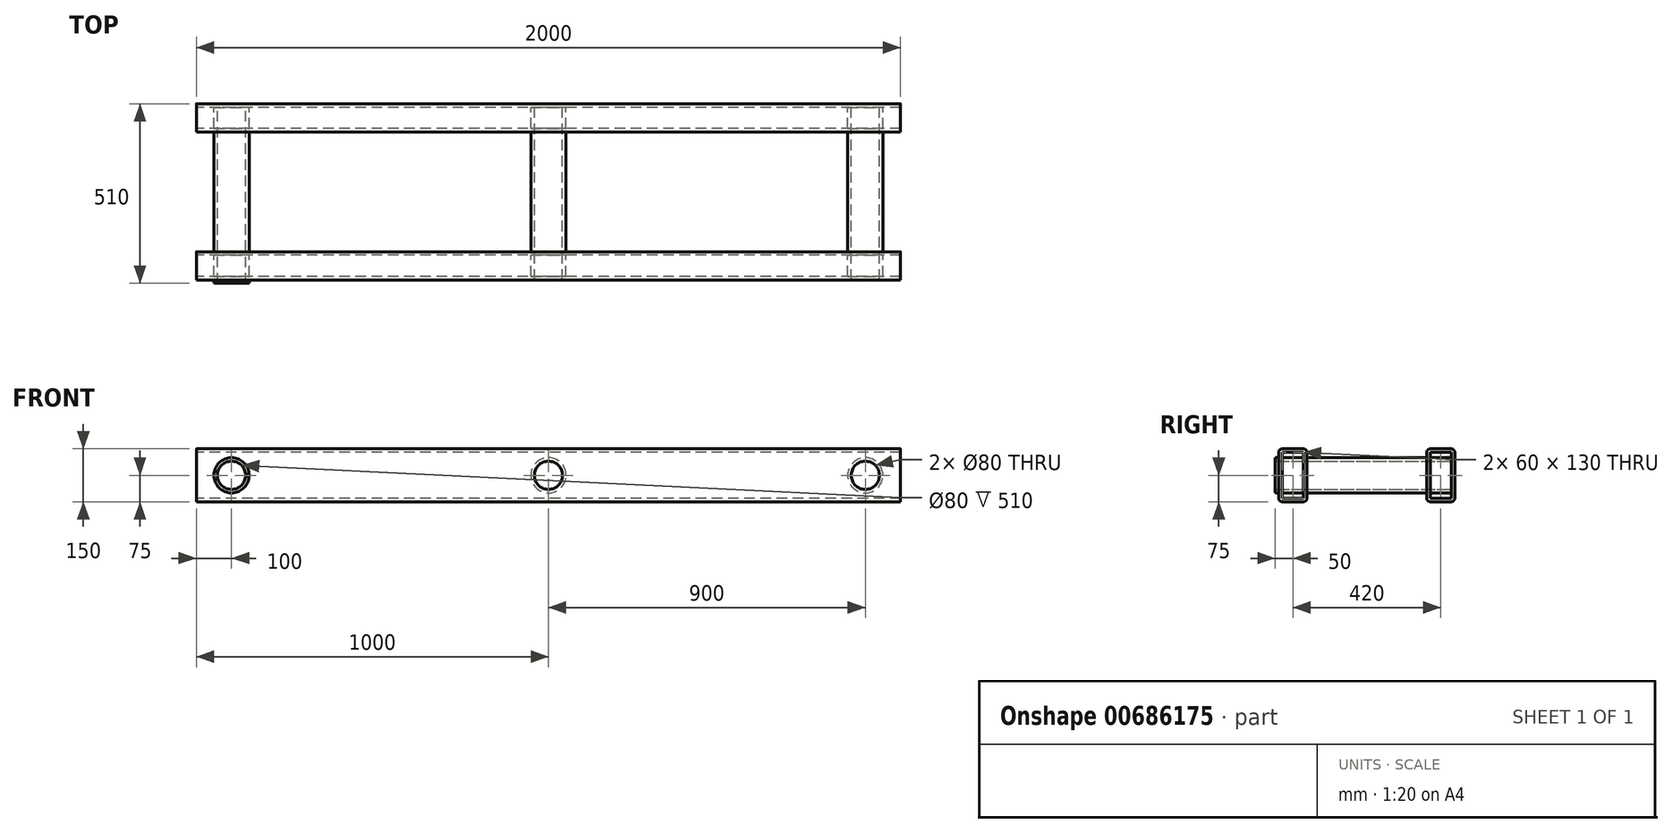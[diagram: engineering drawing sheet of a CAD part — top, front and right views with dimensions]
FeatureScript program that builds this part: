
annotation { "Feature Type Name" : "Feature", "Feature Type Description" : "" }
export const myFeature = defineFeature(function(context is Context, id is Id, definition is map)
    precondition{}
    {
        {
            var Q0;
            Q0=qCreatedBy(makeId("Right.planeOp"),FACE);
            var sketch = newSketch(context, id + "F0", { "sketchPlane" : qUnion([Q0])});
            skLineSegment(sketch, "E0.rect.bottom", {"start": v(-180, -75) * mm, "end": v(-240, -75) * mm});
            skLineSegment(sketch, "E0.rect.top", {"start": v(-180, 75) * mm, "end": v(-240, 75) * mm});
            skLineSegment(sketch, "E0.rect.left", {"start": v(-170, -65) * mm, "end": v(-170, 65) * mm});
            skLineSegment(sketch, "E0.rect.right", {"start": v(-250, -65) * mm, "end": v(-250, 65) * mm});
            skPoint(sketch, "E0.rect.middle", {"position": v(-210, 0) * mm});
            skPoint(sketch, "E1.visualSharp", {"position": v(-250, 75) * mm});
            skArc(sketch, "E1.filletArc", {"start": v(-240, 75) * mm, "mid": v(-247.07, 72.07) * mm, "end": v(-250, 65) * mm});
            skPoint(sketch, "E2.visualSharp", {"position": v(-170, 75) * mm});
            skArc(sketch, "E2.filletArc", {"start": v(-170, 65) * mm, "mid": v(-172.93, 72.07) * mm, "end": v(-180, 75) * mm});
            skPoint(sketch, "E3.visualSharp", {"position": v(-170, -75) * mm});
            skArc(sketch, "E3.filletArc", {"start": v(-180, -75) * mm, "mid": v(-172.93, -72.07) * mm, "end": v(-170, -65) * mm});
            skPoint(sketch, "E4.visualSharp", {"position": v(-250, -75) * mm});
            skArc(sketch, "E4.filletArc", {"start": v(-250, -65) * mm, "mid": v(-247.07, -72.07) * mm, "end": v(-240, -75) * mm});
            skLineSegment(sketch, "E5.0", {"start": v(-180, 65) * mm, "end": v(-240, 65) * mm});
            skLineSegment(sketch, "E5.1", {"start": v(-180, -65) * mm, "end": v(-180, 65) * mm});
            skLineSegment(sketch, "E5.2", {"start": v(-180, -65) * mm, "end": v(-240, -65) * mm});
            skLineSegment(sketch, "E5.3", {"start": v(-240, -65) * mm, "end": v(-240, 65) * mm});
            skArc(sketch, "E6.MirrorCS", {"start": v(240, 75) * mm, "mid": v(247.07, 72.07) * mm, "end": v(250, 65) * mm});
            skArc(sketch, "E7.MirrorCS", {"start": v(170, 65) * mm, "mid": v(172.93, 72.07) * mm, "end": v(180, 75) * mm});
            skArc(sketch, "E8.MirrorCS", {"start": v(250, -65) * mm, "mid": v(247.07, -72.07) * mm, "end": v(240, -75) * mm});
            skArc(sketch, "E9.MirrorCS", {"start": v(180, -75) * mm, "mid": v(172.93, -72.07) * mm, "end": v(170, -65) * mm});
            skLineSegment(sketch, "E10.MirrorCS", {"start": v(180, -75) * mm, "end": v(240, -75) * mm});
            skPoint(sketch, "E11.MirrorP", {"position": v(250, -75) * mm});
            skLineSegment(sketch, "E12.MirrorCS", {"start": v(240, -65) * mm, "end": v(240, 65) * mm});
            skPoint(sketch, "E13.MirrorP", {"position": v(170, 75) * mm});
            skPoint(sketch, "E14.MirrorP", {"position": v(250, 75) * mm});
            skLineSegment(sketch, "E15.MirrorCS", {"start": v(180, -65) * mm, "end": v(240, -65) * mm});
            skPoint(sketch, "E16.MirrorP", {"position": v(210, 0) * mm});
            skLineSegment(sketch, "E17.MirrorCS", {"start": v(180, -65) * mm, "end": v(180, 65) * mm});
            skLineSegment(sketch, "E18.MirrorCS", {"start": v(180, 75) * mm, "end": v(240, 75) * mm});
            skPoint(sketch, "E19.MirrorP", {"position": v(170, -75) * mm});
            skLineSegment(sketch, "E20.MirrorCS", {"start": v(170, -65) * mm, "end": v(170, 65) * mm});
            skLineSegment(sketch, "E21.MirrorCS", {"start": v(180, 65) * mm, "end": v(240, 65) * mm});
            skLineSegment(sketch, "E22.MirrorCS", {"start": v(250, -65) * mm, "end": v(250, 65) * mm});
            skSolve(sketch);
        }
        {
            var Q0;
            Q0=qSketchRegion(id+"F0",true);
            extrude(context, id + "F1", {"entities" : qUnion([Q0]), "endBound" : BoundingType.SYMMETRIC, "depth" : 2000 * mm});
        }
        {
            var Q0;
            Q0=qCreatedBy(makeId("Front.planeOp"),FACE);
            var sketch = newSketch(context, id + "F2", { "sketchPlane" : qUnion([Q0])});
            skCircle(sketch, "E23", {"center": v(900, 0) * mm, "radius": 50 * mm});
            skCircle(sketch, "E24", {"center": v(900, 0) * mm, "radius": 40 * mm});
            skCircle(sketch, "E25.1.0.0", {"center": v(0, 0) * mm, "radius": 50 * mm});
            skCircle(sketch, "E25.1.0.1", {"center": v(0, 0) * mm, "radius": 40 * mm});
            skCircle(sketch, "E25.2.0.0", {"center": v(-900, 0) * mm, "radius": 50 * mm});
            skCircle(sketch, "E25.2.0.1", {"center": v(-900, 0) * mm, "radius": 40 * mm});
            skLineSegment(sketch, "E25.direction1", {"start": v(900, 0) * mm, "end": v(0, 0) * mm, "construction": true});
            skSolve(sketch);
        }
        {
            var Q0;
            Q0=qSketchRegion(id+"F2",true);
            var Q1;
            Q1=makeQuery(id+"F1.opExtrude","SWEPT_FACE",FACE,{"disambiguationData":[OSD([sQuery(id+"F0.wireOp",EDGE,"E0.rect.right")])]});
            var Q2;
            Q2=makeQuery(id+"F1.opExtrude","SWEPT_FACE",FACE,{"disambiguationData":[OSD([sQuery(id+"F0.wireOp",EDGE,"E22.MirrorCS")])]});
            extrude(context, id + "F3", {"entities" : qUnion([Q0]), "operationType" : NewBodyOperationType.ADD, "endBound" : BoundingType.UP_TO_SURFACE, "endBoundEntityFace" : qUnion([Q1]), "depth" : 25 * mm, "hasSecondDirection" : true, "secondDirectionBound" : SecondDirectionBoundingType.UP_TO_SURFACE, "secondDirectionOppositeDirection" : true, "secondDirectionBoundEntityFace" : qUnion([Q2]), "secondDirectionDepth" : 25 * mm});
        }
        {
            var Q0;
            Q0=makeQuery(id+"F2.imprint","IMPRINT",FACE,{"disambiguationData":[TD([[makeQuery(id+"F2.imprint","IMPRINT",EDGE,{"derivedFrom":sQuery(id+"F2.wireOp",EDGE,"E24")}),1.0]])]});
            var Q1;
            Q1=makeQuery(id+"F2.imprint","IMPRINT",FACE,{"disambiguationData":[TD([[makeQuery(id+"F2.imprint","IMPRINT",EDGE,{"derivedFrom":sQuery(id+"F2.wireOp",EDGE,"E25.1.0.1")}),1.0]])]});
            var Q2;
            Q2=makeQuery(id+"F2.imprint","IMPRINT",FACE,{"disambiguationData":[TD([[makeQuery(id+"F2.imprint","IMPRINT",EDGE,{"derivedFrom":sQuery(id+"F2.wireOp",EDGE,"E25.2.0.1")}),1.0]])]});
            extrude(context, id + "F4", {"entities" : qUnion([Q0, Q1, Q2]), "operationType" : NewBodyOperationType.REMOVE, "endBound" : BoundingType.THROUGH_ALL, "oppositeDirection" : true, "depth" : 25 * mm, "hasSecondDirection" : true, "secondDirectionBound" : SecondDirectionBoundingType.THROUGH_ALL, "secondDirectionOppositeDirection" : false, "secondDirectionDepth" : 25 * mm});
        }
        {
            var Q0;
            Q0=makeQuery(id+"F2.imprint","IMPRINT",FACE,{"disambiguationData":[TD([[makeQuery(id+"F2.imprint","IMPRINT",EDGE,{"derivedFrom":sQuery(id+"F2.wireOp",EDGE,"E25.2.0.0")}),1.0]])]});
            var Q1;
            Q1=makeQuery(id+"F1.opExtrude","SWEPT_FACE",FACE,{"disambiguationData":[OSD([sQuery(id+"F0.wireOp",EDGE,"E0.rect.right")])]});
            extrude(context, id + "F5", {"entities" : qUnion([Q0]), "operationType" : NewBodyOperationType.ADD, "depth" : 260 * mm, "hasSecondDirection" : true, "secondDirectionBound" : SecondDirectionBoundingType.UP_TO_SURFACE, "secondDirectionOppositeDirection" : false, "secondDirectionBoundEntityFace" : qUnion([Q1]), "secondDirectionDepth" : 25 * mm});
        }
    });
